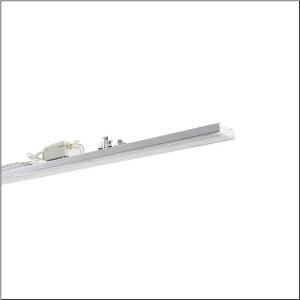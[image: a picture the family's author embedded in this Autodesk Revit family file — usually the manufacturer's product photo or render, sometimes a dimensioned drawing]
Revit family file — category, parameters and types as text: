
# Revit family: licross_r__21_recessed_mo_52tl10de45xg_9f5a
name_source: partatom
category: Lighting Fixtures
units: mm (PartAtom-declared; Revit-internal decimal feet)

## family parameters
Cut with Voids When Loaded = No
Host = Face
Light Source = No
Part Type = Normal
Room Calculation Point = No
Round Connector Dimension = Use Diameter
Shared = No

## types (1)
- --- (1 x LED, 5000 lm, 29.9 W, 4000K)
    Apparent Load = 30 VA
    CIE Flux Codes = 50 81 96 100 100
    Color Rendering = 80
    Color Temperature = 4000K
    Default Elevation = 1800 mm
    Description = Licross® 21 Recessed MO, luminaire insert, of sheet steel, galvanised, coil coated, white, length: 750mm, width: 66mm, height: 67mm, LED rated luminous flux: 5.000lm, light colour: 840, control gear: DALI 2, with plug, 5-pole, with phase selection, mains connection: 220..240V, AC, 50/60Hz, rated input power: 30W, halogen-free wiring, primary optical cover: cover, of PMMA, light emission: direct distribution, primary light characteristic: symmetric, protection rating (complete): IP40, insulation class (complete): insulation class I (protective earthing), certification: CE, ENEC, VDE, UKCA, protection symbol: D if used in an environment without relevant dust loads with corresponding accessories, impact resistance: IK06, permissible ambient temperature for indoor applications: -25..+35°C, corresponds to IFS (International Featured Standards) requirements for safety and quality in the food industry, reducing of maximum allowable ambient temperature of 5°C with ceiling mounting, LABS conformity tested according to VDMA 24364:2018-05, packaging unit: 1 piece
    Height = 58 mm
    Lamp = 1 x LED
    Lamp Light Flux = 5000 lm
    Lamp Power = 29.9 W
    Lamp count = 1
    Length = 750 mm
    Luminous efficacy = 167 lm/W
    Manufacturer = Siteco
    ModVariant = No
    Model = 52TL10DE45XG
    Mounting Place = Ceiling
    Mounting Type = Pendant
    Number of Poles = 1
    OnlyDefault = Yes
    Power Factor = 1
    Product Name = Licross® 21 Recessed MO
    Product group = luminaire insert
    ProductGroupID = 901
    Protection Class = Protection class I
    Protection Degree = IP 40
    RLX_Detail_Level = 1
    RLX_Emergency_Light_Flux = 0 lm
    RLX_Emergency_Type = 0
    RLX_Emergency_Type_DB = No
    RlxData = <blob elided: 28645 chars, md5=0af754dd>
    Socket = socket
    Standby Power = 0 W
    System Light Flux = 5000 lm
    System Power = 30 W
    Type Comments = factory setting: luminous flux: 100 % | dim-lin: 254 | 390 mA
    Type Image = l_1296930.jpg
    URL = http://relux.com
    VarID = @adj_059287
    Voltage = 0 V
    Weight = 0.00 kg
    Width = 66 mm

## geometry (parser evidence)
native form markers: Blend x4, Sweep x9
no freeform markers — native parametric forms only
